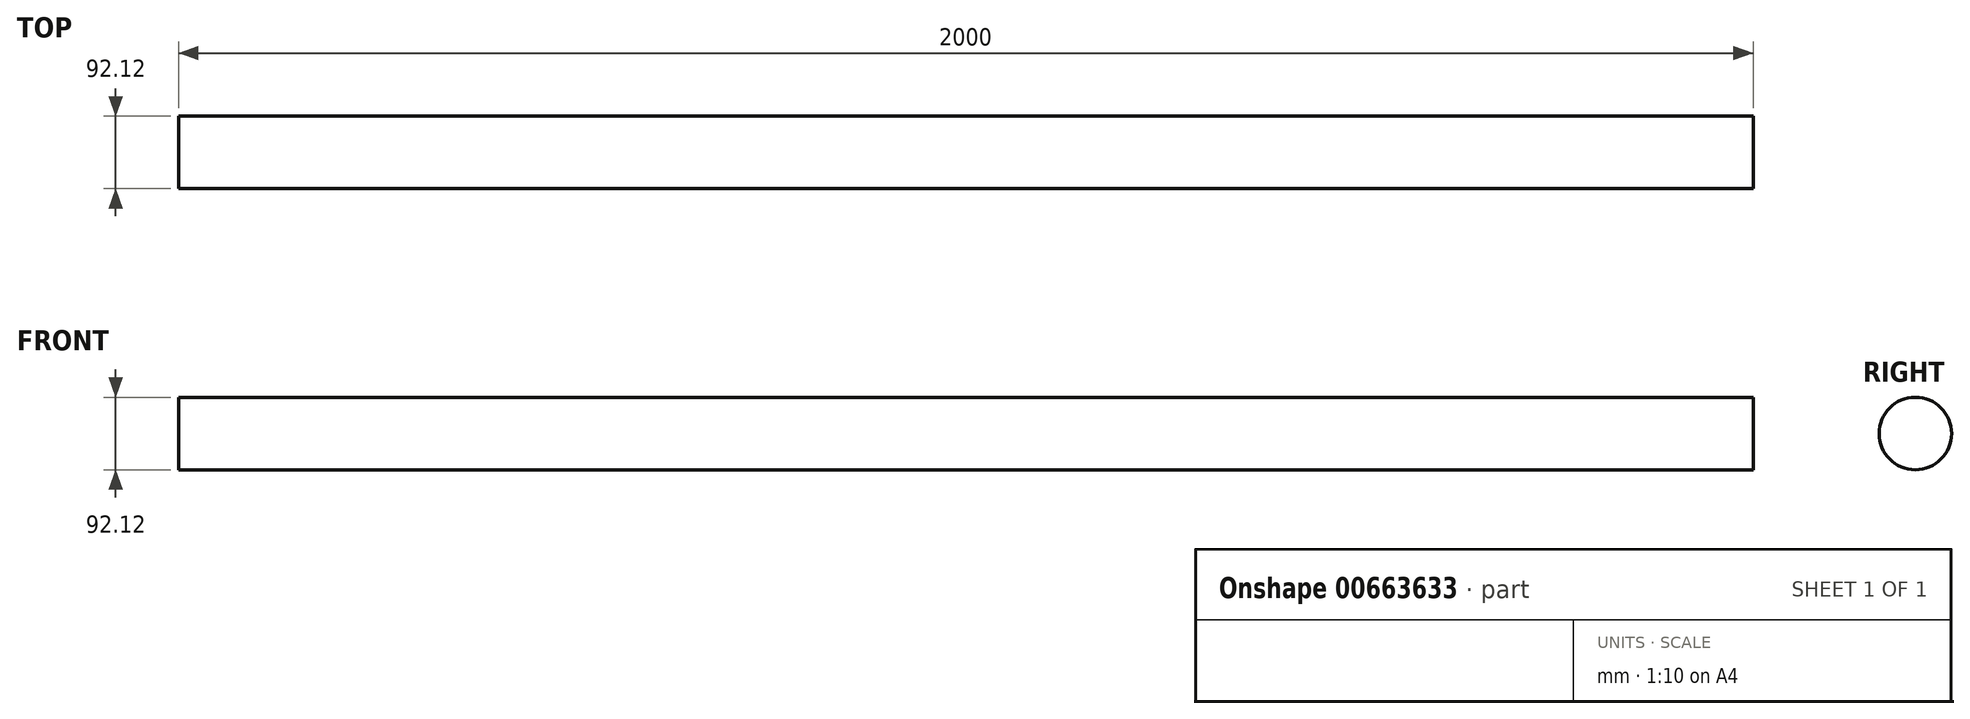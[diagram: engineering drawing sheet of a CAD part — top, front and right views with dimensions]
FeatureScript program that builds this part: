
annotation { "Feature Type Name" : "Feature", "Feature Type Description" : "" }
export const myFeature = defineFeature(function(context is Context, id is Id, definition is map)
    precondition{}
    {
        {
            var Q0;
            Q0=qCreatedBy(makeId("Right.planeOp"),FACE);
            var sketch = newSketch(context, id + "F0", { "sketchPlane" : qUnion([Q0])});
            skCircle(sketch, "E0", {"center": v(-7.22, 8.3) * mm, "radius": 46.06 * mm});
            skSolve(sketch);
        }
        {
            var Q0;
            Q0=makeQuery(id+"F0.imprint","IMPRINT",FACE,{"disambiguationData":[TD([[makeQuery(id+"F0.imprint","IMPRINT",EDGE,{"derivedFrom":sQuery(id+"F0.wireOp",EDGE,"E0")}),1.0]])]});
            extrude(context, id + "F1", {"entities" : qUnion([Q0]), "depth" : 2000 * mm, "offsetDistance" : 25.4 * mm});
        }
    });
